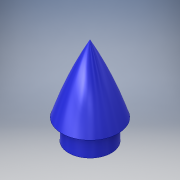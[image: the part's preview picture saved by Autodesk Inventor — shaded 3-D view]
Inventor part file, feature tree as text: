
AUTODESK INVENTOR PART (.ipt)
format: ipt  version: 2018 (Build 220112000, 112)  size: 154,624 bytes
history: native  units: in
note: dims shown in document units (in); Inventor stores cm internally (conversion verified against a paired STEP export)
features: sketch x2, revolve x1, shell x1, extrude x1
ambient origin geometry x8: Origin, YZ Plane, XZ Plane, XY Plane, X Axis, Y Axis, Z Axis, Center Point
bodies: Solid1 (feature_tree)
feature tree (5):
  revolve  "Revolution1"  [1 undecoded]
  shell  "Shell1"  Thickness=14.0in
  extrude  "Extrusion1"  Depth=0.25in
  sketch  "Sketch1"  dims[d0=1.5625in d1=5.0in d3=14.0in]
  sketch  "Sketch2"  dims[d4=90.0deg d5=1.5in d6=1.5in d7=2.5in d9=0.75in d10=0.25in d11=0.75in d12=0.25in d13=0.25in d14=0.25in d15=0.5in d16=0.0in]
note: 1 required parameter value undecoded (feature->parameter linkage not recoverable at this tier; creation-order binding heuristic only, values carry confidence <= 0.55)
